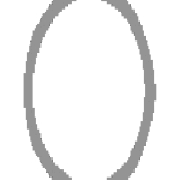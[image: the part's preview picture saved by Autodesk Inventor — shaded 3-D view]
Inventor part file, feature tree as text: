
AUTODESK INVENTOR PART (.ipt)
format: ipt  version: 2021 (Build 250183000, 183)  size: 117,760 bytes
history: native  units: in
note: dims shown in document units (in); Inventor stores cm internally (conversion verified against a paired STEP export)
features: other x4, plane x3, sketch x3, split x2
ambient origin geometry x8: Origin, YZ Plane, XZ Plane, XY Plane, X Axis, Y Axis, Z Axis, Center Point
bodies: Solid1 (feature_tree), Body (feature_tree)
feature tree (12):
  other  "Driven Length"
  other  "Frame Generator"
  other  "Start Plane"
  other  "End Plane"
  plane  "Work Plane5"
  split  "Split1"
  plane  "Work Plane6"
  split  "Split2"
  sketch  "Sketch"  dims[d2=28.9in d4=-0.3536in d5=28.9in d6=0.12in d7=0.0in d10=90.0deg d9=29.2536in]
  sketch  "Sketch4"  dims[d0=1.0in]
  plane  "Work Plane4"
  sketch  "Sketch5"  dims[d1=0.065in]
